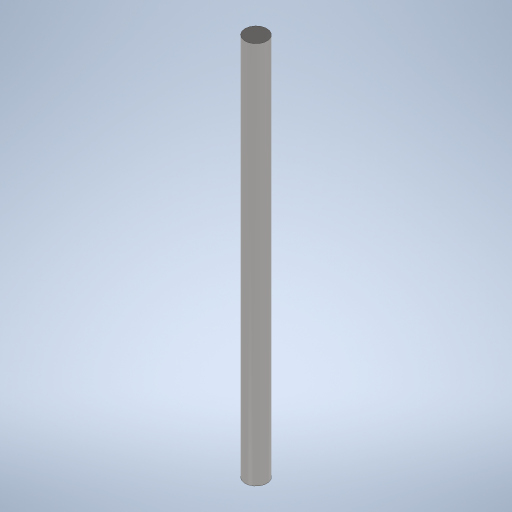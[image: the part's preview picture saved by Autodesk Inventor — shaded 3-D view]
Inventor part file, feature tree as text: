
AUTODESK INVENTOR PART (.ipt)
format: ipt  version: 2023.1 (Build 271208000, 208)  size: 229,888 bytes
history: native  units: mm
features: extrude x1, sketch x1
ambient origin geometry x8: Origin, YZ Plane, XZ Plane, XY Plane, X Axis, Y Axis, Z Axis, Center Point
bodies: Solid1 (feature_tree)
feature tree (2):
  extrude  "Extrusion1"  Depth=70.0mm TaperAngle=0.0deg
  sketch  "Sketch1"  dims[d0=4.0mm d1=70.0mm d2=0.0mm]
